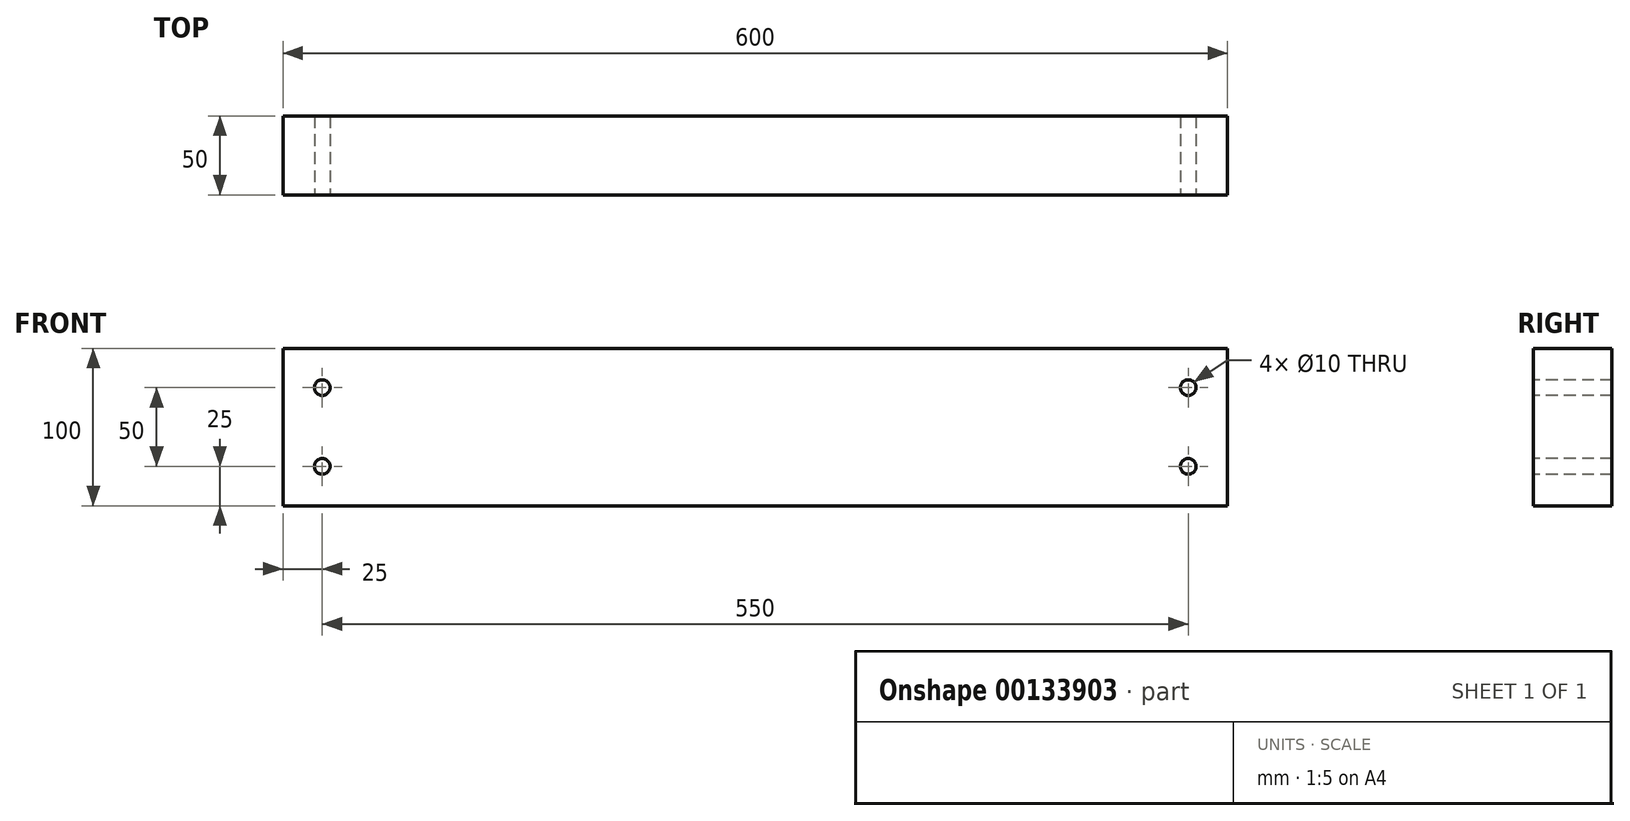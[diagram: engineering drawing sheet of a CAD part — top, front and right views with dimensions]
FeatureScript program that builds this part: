
annotation { "Feature Type Name" : "Feature", "Feature Type Description" : "" }
export const myFeature = defineFeature(function(context is Context, id is Id, definition is map)
    precondition{}
    {
        {
            var Q0;
            Q0=qCreatedBy(makeId("Front.planeOp"),FACE);
            var sketch = newSketch(context, id + "F0", { "sketchPlane" : qUnion([Q0])});
            skLineSegment(sketch, "E0.bottom", {"start": v(300, -50) * mm, "end": v(-300, -50) * mm});
            skLineSegment(sketch, "E0.top", {"start": v(300, 50) * mm, "end": v(-300, 50) * mm});
            skLineSegment(sketch, "E0.left", {"start": v(300, -50) * mm, "end": v(300, 50) * mm});
            skLineSegment(sketch, "E0.right", {"start": v(-300, -50) * mm, "end": v(-300, 50) * mm});
            skPoint(sketch, "E0.middle", {"position": v(0, 0) * mm});
            skSolve(sketch);
        }
        {
            var Q0;
            Q0=qSketchRegion(id+"F0",true);
            extrude(context, id + "F1", {"entities" : qUnion([Q0]), "depth" : 50 * mm});
        }
        {
            var Q0;
            Q0=makeQuery(id+"F1.opExtrude","CAP_FACE",FACE,{"disambiguationData":[OSD([sQuery(id+"F0.wireOp",EDGE,"E0.bottom"),sQuery(id+"F0.wireOp",EDGE,"E0.top"),sQuery(id+"F0.wireOp",EDGE,"E0.left"),sQuery(id+"F0.wireOp",EDGE,"E0.right")])],"isStart":false});
            var sketch = newSketch(context, id + "F2", { "sketchPlane" : qUnion([Q0])});
            skCircle(sketch, "E1", {"center": v(-275, 25) * mm, "radius": 5 * mm});
            skCircle(sketch, "E2", {"center": v(-275, -25) * mm, "radius": 5 * mm});
            skCircle(sketch, "E3", {"center": v(275, 25) * mm, "radius": 5 * mm});
            skCircle(sketch, "E4", {"center": v(275, -25) * mm, "radius": 5 * mm});
            skSolve(sketch);
        }
        {
            var Q0;
            Q0=makeQuery(id+"F2.imprint","IMPRINT",FACE,{"disambiguationData":[TD([[makeQuery(id+"F2.imprint","IMPRINT",EDGE,{"derivedFrom":sQuery(id+"F2.wireOp",EDGE,"E1")}),1.0]])]});
            var Q1;
            Q1=makeQuery(id+"F2.imprint","IMPRINT",FACE,{"disambiguationData":[TD([[makeQuery(id+"F2.imprint","IMPRINT",EDGE,{"derivedFrom":sQuery(id+"F2.wireOp",EDGE,"E2")}),1.0]])]});
            var Q2;
            Q2=makeQuery(id+"F2.imprint","IMPRINT",FACE,{"disambiguationData":[TD([[makeQuery(id+"F2.imprint","IMPRINT",EDGE,{"derivedFrom":sQuery(id+"F2.wireOp",EDGE,"E3")}),1.0]])]});
            var Q3;
            Q3=makeQuery(id+"F2.imprint","IMPRINT",FACE,{"disambiguationData":[TD([[makeQuery(id+"F2.imprint","IMPRINT",EDGE,{"derivedFrom":sQuery(id+"F2.wireOp",EDGE,"E4")}),1.0]])]});
            extrude(context, id + "F3", {"entities" : qUnion([Q0, Q1, Q2, Q3]), "operationType" : NewBodyOperationType.REMOVE, "endBound" : BoundingType.THROUGH_ALL, "oppositeDirection" : true, "depth" : 25 * mm});
        }
    });
